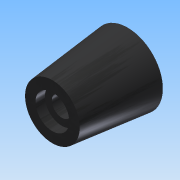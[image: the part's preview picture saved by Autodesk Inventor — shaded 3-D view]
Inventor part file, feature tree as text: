
AUTODESK INVENTOR PART (.ipt)
format: ipt  version: 2015 (Build 190159000, 159)  size: 117,248 bytes
history: native  units: mm
features: sketch x3, extrude x2, other x1
ambient origin geometry x8: Origin, YZ Plane, XZ Plane, XY Plane, X Axis, Y Axis, Z Axis, Center Point
bodies: Body1 (feature_tree)
feature tree (6):
  extrude  "Extrusion3"  Depth=4.25mm
  other  "Dépouille de face1"
  sketch  "Esquisse4"
  extrude  "Extrusion5"  Depth=15.0mm
  sketch  "Esquisse3"
  sketch  "Esquisse6"
